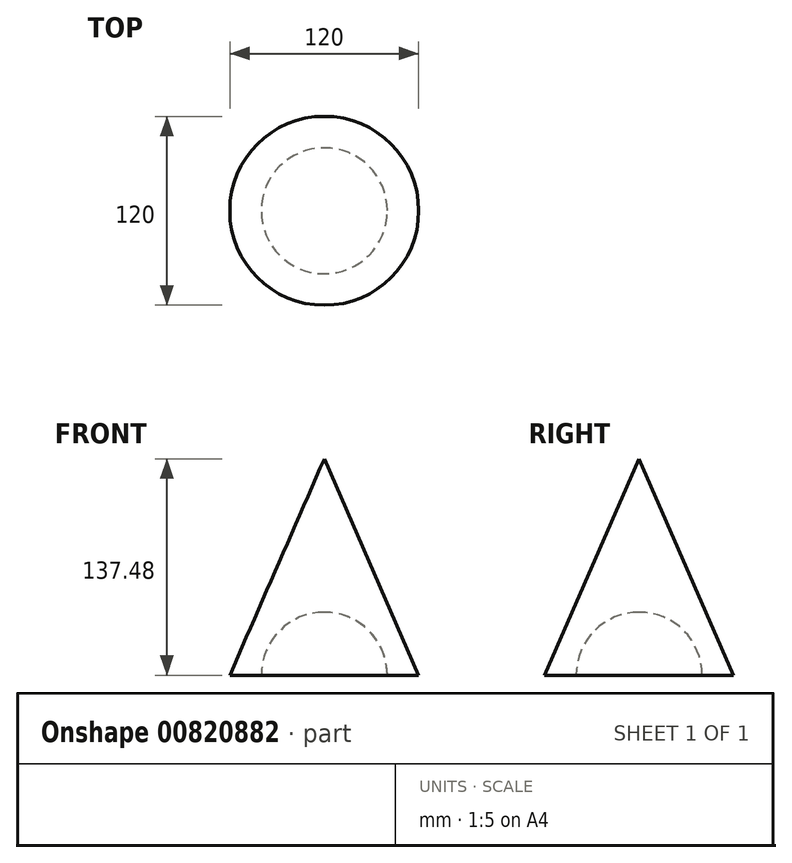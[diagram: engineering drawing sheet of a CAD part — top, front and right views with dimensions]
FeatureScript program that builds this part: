
annotation { "Feature Type Name" : "Feature", "Feature Type Description" : "" }
export const myFeature = defineFeature(function(context is Context, id is Id, definition is map)
    precondition{}
    {
        {
            var Q0;
            Q0=qCreatedBy(makeId("Front.planeOp"),FACE);
            var sketch = newSketch(context, id + "F0", { "sketchPlane" : qUnion([Q0])});
            skLineSegment(sketch, "E0", {"start": v(40, 0) * mm, "end": v(60, 0) * mm});
            skLineSegment(sketch, "E1", {"start": v(60, 0) * mm, "end": v(0, 137.48) * mm});
            skLineSegment(sketch, "E2", {"start": v(0, -51.38) * mm, "end": v(0, 151.48) * mm, "construction": true});
            skArc(sketch, "E3", {"start": v(40, 0) * mm, "mid": v(28.28, 28.28) * mm, "end": v(0, 40) * mm});
            skLineSegment(sketch, "E4", {"start": v(0, 0) * mm, "end": v(-40, 0) * mm, "construction": true});
            skSolve(sketch);
        }
        {
            var Q0;
            Q0=sQuery(id+"F0.wireOp",EDGE,"E3");
            var Q1;
            Q1=sQuery(id+"F0.wireOp",EDGE,"E0");
            var Q2;
            Q2=sQuery(id+"F0.wireOp",EDGE,"E1");
            var Q3;
            Q3=sQuery(id+"F0.wireOp",EDGE,"E2");
            revolve(context, id + "F1", {"bodyType" : ToolBodyType.SURFACE, "surfaceOperationType" : NewSurfaceOperationType.NEW, "surfaceEntities" : qUnion([Q0, Q1, Q2]), "axis" : qUnion([Q3]), "revolveType" : RevolveType.FULL});
        }
    });
